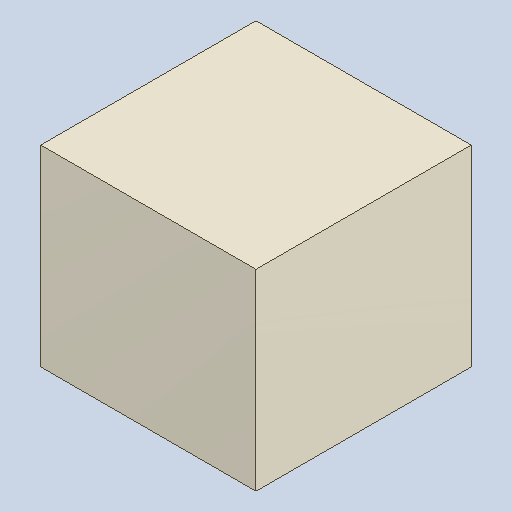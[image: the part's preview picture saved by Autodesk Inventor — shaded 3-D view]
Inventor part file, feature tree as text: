
AUTODESK INVENTOR PART (.ipt)
format: ipt  version: 2023.4 (Build 274418000, 418)  size: 81,920 bytes
history: native  units: mm
features: extrude x1
ambient origin geometry x8: Origin, YZ Plane, XZ Plane, XY Plane, X Axis, Y Axis, Z Axis, Center Point
bodies: Solid1 (feature_tree)
feature tree (1):
  extrude  "Extruded"  [1 undecoded]
note: 1 required parameter value undecoded (feature->parameter linkage not recoverable at this tier; creation-order binding heuristic only, values carry confidence <= 0.55)
